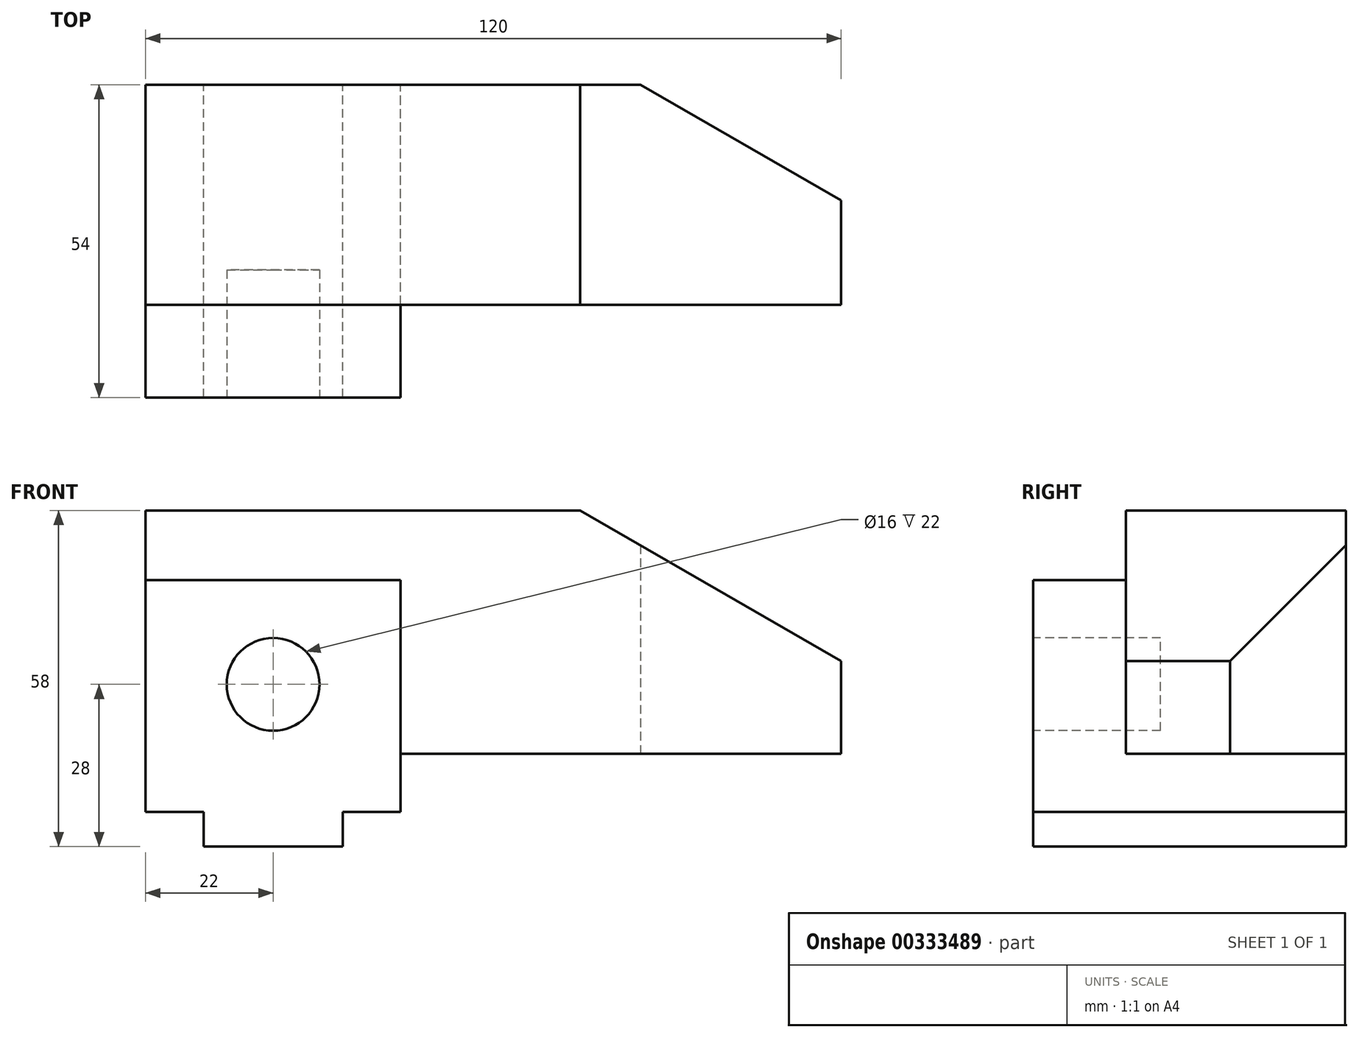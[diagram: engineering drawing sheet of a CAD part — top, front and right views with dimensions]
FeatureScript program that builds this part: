
annotation { "Feature Type Name" : "Feature", "Feature Type Description" : "" }
export const myFeature = defineFeature(function(context is Context, id is Id, definition is map)
    precondition{}
    {
        {
            var Q0;
            Q0=qCreatedBy(makeId("Front.planeOp"),FACE);
            var sketch = newSketch(context, id + "F0", { "sketchPlane" : qUnion([Q0])});
            skLineSegment(sketch, "E0", {"start": v(0, 6) * mm, "end": v(10, 6) * mm});
            skLineSegment(sketch, "E1", {"start": v(10, 6) * mm, "end": v(10, 0) * mm});
            skLineSegment(sketch, "E2", {"start": v(10, 0) * mm, "end": v(34, 0) * mm});
            skLineSegment(sketch, "E3", {"start": v(34, 0) * mm, "end": v(34, 6) * mm});
            skLineSegment(sketch, "E4", {"start": v(34, 6) * mm, "end": v(44, 6) * mm});
            skLineSegment(sketch, "E5", {"start": v(44, 6) * mm, "end": v(44, 46) * mm});
            skLineSegment(sketch, "E6", {"start": v(44, 46) * mm, "end": v(0, 46) * mm});
            skLineSegment(sketch, "E7", {"start": v(0, 46) * mm, "end": v(0, 6) * mm});
            skLineSegment(sketch, "E8", {"start": v(0, 46) * mm, "end": v(0, 58) * mm});
            skLineSegment(sketch, "E9", {"start": v(0, 58) * mm, "end": v(75, 58) * mm});
            skCircle(sketch, "E10", {"center": v(22, 28) * mm, "radius": 8 * mm});
            skLineSegment(sketch, "E11", {"start": v(120, 16) * mm, "end": v(120, 32.02) * mm});
            skLineSegment(sketch, "E12", {"start": v(120, 32.02) * mm, "end": v(75, 58) * mm});
            skLineSegment(sketch, "E13", {"start": v(120, 16) * mm, "end": v(0, 16) * mm});
            skSolve(sketch);
        }
        {
            var Q0;
            Q0=makeQuery(id+"F0.imprint","IMPRINT",FACE,{"disambiguationData":[TD([[makeQuery(id+"F0.imprint","IMPRINT",EDGE,{"derivedFrom":sQuery(id+"F0.wireOp",EDGE,"E0")}),1.0]])]});
            var Q1;
            {var subQ1=sQuery(id+"F0.wireOp",EDGE,"E6");Q1=makeQuery(id+"F0.imprint","IMPRINT",FACE,{"disambiguationData":[TD([[makeQuery(id+"F0.imprint","IMPRINT",EDGE,{"derivedFrom":subQ1}),1.0]])]});}
            var Q2;
            Q2=makeQuery(id+"F0.imprint","IMPRINT",FACE,{"disambiguationData":[TD([[makeQuery(id+"F0.imprint","IMPRINT",EDGE,{"derivedFrom":sQuery(id+"F0.wireOp",EDGE,"E10")}),1.0]])]});
            extrude(context, id + "F1", {"entities" : qUnion([Q0, Q1, Q2]), "depth" : 54 * mm});
        }
        {
            var Q0;
            {var subQ0=sQuery(id+"F0.wireOp",EDGE,"E6");Q0=makeQuery(id+"F0.imprint","IMPRINT",FACE,{"disambiguationData":[TD([[makeQuery(id+"F0.imprint","IMPRINT",EDGE,{"derivedFrom":subQ0}),-1.0]])]});}
            extrude(context, id + "F2", {"entities" : qUnion([Q0]), "operationType" : NewBodyOperationType.ADD, "depth" : 38 * mm});
        }
        {
            var Q0;
            Q0=makeQuery(id+"F1.opExtrude","CAP_FACE",FACE,{"disambiguationData":[OSD([sQuery(id+"F0.wireOp",EDGE,"E0"),sQuery(id+"F0.wireOp",EDGE,"E1"),sQuery(id+"F0.wireOp",EDGE,"E2"),sQuery(id+"F0.wireOp",EDGE,"E3"),sQuery(id+"F0.wireOp",EDGE,"E4"),sQuery(id+"F0.wireOp",EDGE,"E5"),sQuery(id+"F0.wireOp",EDGE,"E6"),sQuery(id+"F0.wireOp",EDGE,"E7")])],"isStart":false});
            var sketch = newSketch(context, id + "F3", { "sketchPlane" : qUnion([Q0])});
            skCircle(sketch, "E14", {"center": v(22, 28) * mm, "radius": 8 * mm});
            skSolve(sketch);
        }
        {
            var Q0;
            Q0=makeQuery(id+"F3.imprint","IMPRINT",FACE,{"disambiguationData":[TD([[makeQuery(id+"F3.imprint","IMPRINT",EDGE,{"derivedFrom":sQuery(id+"F3.wireOp",EDGE,"E14")}),1.0]])]});
            extrude(context, id + "F4", {"entities" : qUnion([Q0]), "operationType" : NewBodyOperationType.REMOVE, "oppositeDirection" : true, "depth" : 22 * mm});
        }
        {
            var Q0;
            Q0=makeQuery(id+"F2.opExtrude","SWEPT_FACE",FACE,{"disambiguationData":[OSD([sQuery(id+"F0.wireOp",EDGE,"E13")])]});
            var sketch = newSketch(context, id + "F5", { "sketchPlane" : qUnion([Q0])});
            skLineSegment(sketch, "E15", {"start": v(120, 0) * mm, "end": v(85.36, 0) * mm});
            skLineSegment(sketch, "E16", {"start": v(120, 0) * mm, "end": v(120, 20) * mm});
            skLineSegment(sketch, "E17", {"start": v(120, 20) * mm, "end": v(85.36, 0) * mm});
            skSolve(sketch);
        }
        {
            var Q0;
            Q0 = qSketchRegion(id + "F5", true);
            extrude(context, id + "F6", {"entities" : qUnion([Q0]), "operationType" : NewBodyOperationType.REMOVE, "endBound" : BoundingType.THROUGH_ALL, "oppositeDirection" : true, "depth" : 25 * mm});
        }
    });
